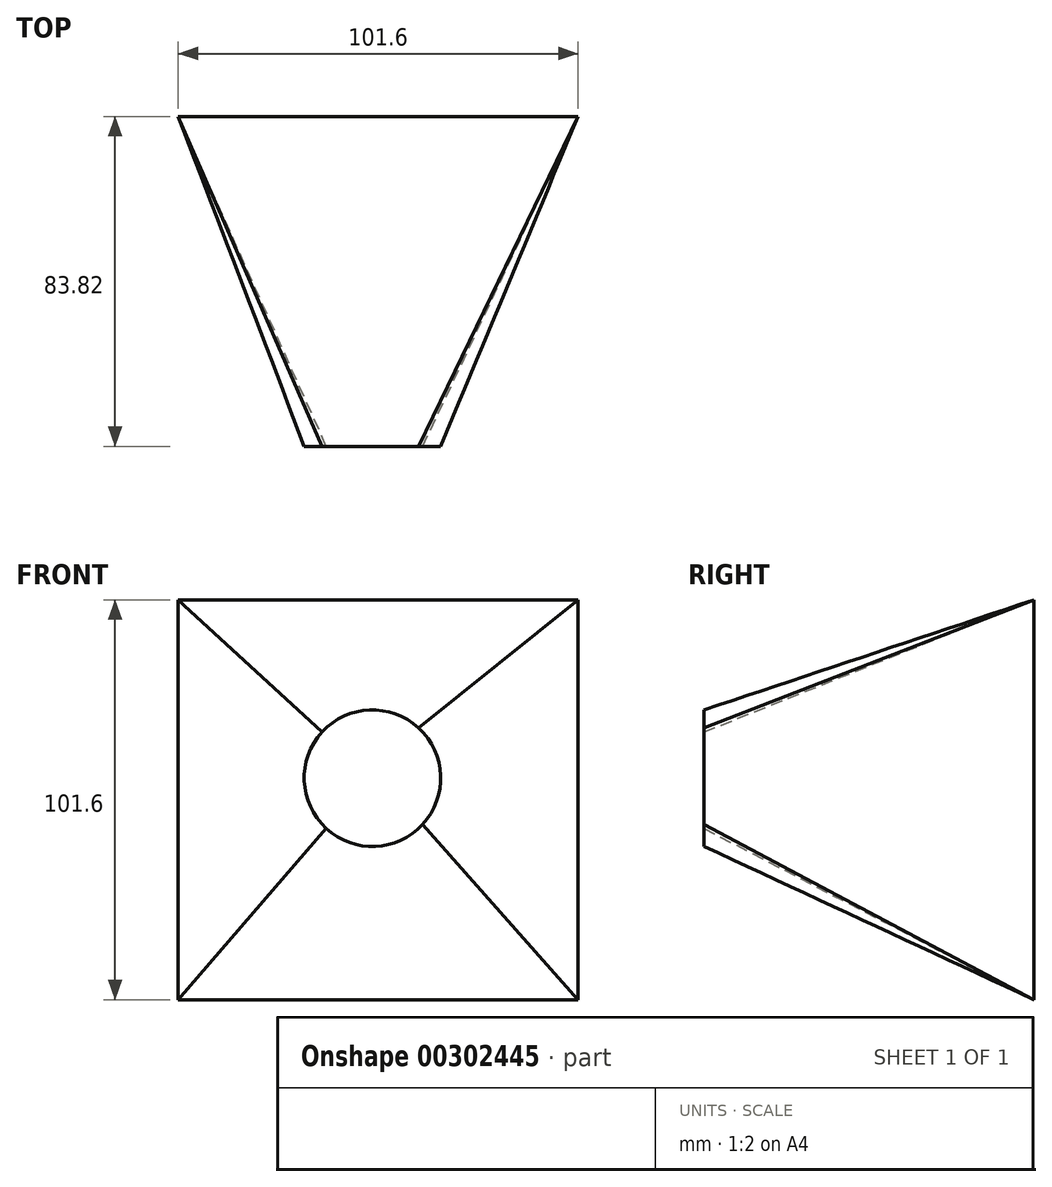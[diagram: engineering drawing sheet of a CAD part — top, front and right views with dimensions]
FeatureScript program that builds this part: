
annotation { "Feature Type Name" : "Feature", "Feature Type Description" : "" }
export const myFeature = defineFeature(function(context is Context, id is Id, definition is map)
    precondition{}
    {
        {
            var Q0;
            Q0=qCreatedBy(makeId("Front.planeOp"),FACE);
            var sketch = newSketch(context, id + "F0", { "sketchPlane" : qUnion([Q0])});
            skLineSegment(sketch, "E0.bottom", {"start": v(-49.35, 45.33) * mm, "end": v(52.25, 45.33) * mm});
            skLineSegment(sketch, "E0.top", {"start": v(-49.35, -56.27) * mm, "end": v(52.25, -56.27) * mm});
            skLineSegment(sketch, "E0.left", {"start": v(-49.35, 45.33) * mm, "end": v(-49.35, -56.27) * mm});
            skLineSegment(sketch, "E0.right", {"start": v(52.25, 45.33) * mm, "end": v(52.25, -56.27) * mm});
            skPoint(sketch, "E1.oppositeSnap0", {"position": v(1.45, 45.33) * mm});
            skLineSegment(sketch, "E1.bottom", {"start": v(4, 52.57) * mm, "end": v(1.45, 52.57) * mm});
            skLineSegment(sketch, "E1.top", {"start": v(4, 52.57) * mm, "end": v(1.45, 52.57) * mm});
            skLineSegment(sketch, "E1.left", {"start": v(4, 52.57) * mm, "end": v(4, 52.57) * mm});
            skLineSegment(sketch, "E1.right", {"start": v(1.45, 52.57) * mm, "end": v(1.45, 52.57) * mm});
            skSolve(sketch);
        }
        {
            var Q0;
            Q0=makeQuery(id+"F0.imprint","IMPRINT",FACE,{"disambiguationData":[TD([[makeQuery(id+"F0.imprint","IMPRINT",EDGE,{"derivedFrom":sQuery(id+"F0.wireOp",EDGE,"E0.bottom")}),-1.0]])]});
            cPlane(context, id + "F1", {"entities" : qUnion([Q0]), "cplaneType" : CPlaneType.OFFSET, "offset" : 83.82 * mm, "width" : 152.4 * mm, "height" : 152.4 * mm});
        }
        {
            var Q0;
            Q0=qCreatedBy(id+"F1.planeOp",FACE);
            var sketch = newSketch(context, id + "F2", { "sketchPlane" : qUnion([Q0])});
            skCircle(sketch, "E2", {"center": v(0, 0) * mm, "radius": 17.34 * mm});
            skSolve(sketch);
        }
        {
            var Q0;
            Q0=makeQuery(id+"F2.imprint","IMPRINT",FACE,{"disambiguationData":[TD([[makeQuery(id+"F2.imprint","IMPRINT",EDGE,{"derivedFrom":sQuery(id+"F2.wireOp",EDGE,"E2")}),1.0]])]});
            var Q1;
            Q1=makeQuery(id+"F0.imprint","IMPRINT",FACE,{"disambiguationData":[TD([[makeQuery(id+"F0.imprint","IMPRINT",EDGE,{"derivedFrom":sQuery(id+"F0.wireOp",EDGE,"E0.bottom")}),-1.0]])]});
            loft(context, id + "F3", {"sheetProfilesArray" : [{ "sheetProfileEntities" : qUnion([Q0]) }, { "sheetProfileEntities" : qUnion([Q1]) }]});
        }
    });
